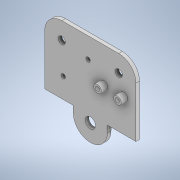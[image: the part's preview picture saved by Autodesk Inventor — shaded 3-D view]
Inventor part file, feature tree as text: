
AUTODESK INVENTOR PART (.ipt)
format: ipt  version: 2022 (Build 260153070, 153G)  size: 169,472 bytes
history: native  units: mm
features: extrude x3, sketch x1
ambient origin geometry x8: Origin, YZ Plane, XZ Plane, XY Plane, X Axis, Y Axis, Z Axis, Center Point
bodies: Solid1 (feature_tree)
feature tree (4):
  sketch  "Sketch1"  dims[d0=7.2mm d1=52.1mm d2=4.6mm d3=32.0mm d4=32.0mm d5=4.0mm d6=33.25mm d7=19.0mm d8=4.0mm d9=1.5mm d10=14.35mm d11=3.0mm d12=9.5mm d13=24.45mm d14=3.0mm d15=23.5mm d16=1.2mm d17=1.2mm d18=20.0mm d19=11.9mm d20=5.0mm d21=3.0mm d22=3.0mm d23=5.0mm d24=20.0mm d25=12.0mm d27=12.0mm d28=2.5mm d29=0.0mm d30=7.0mm d31=0.0mm d32=2.5mm d33=1.5mm d34=0.0mm d35=0.0mm]
  extrude  "Extrusion1"  Depth=1.5mm
  extrude  "Extrusion2"  Depth=1.5mm
  extrude  "Extrusion3"  Depth=1.5mm
